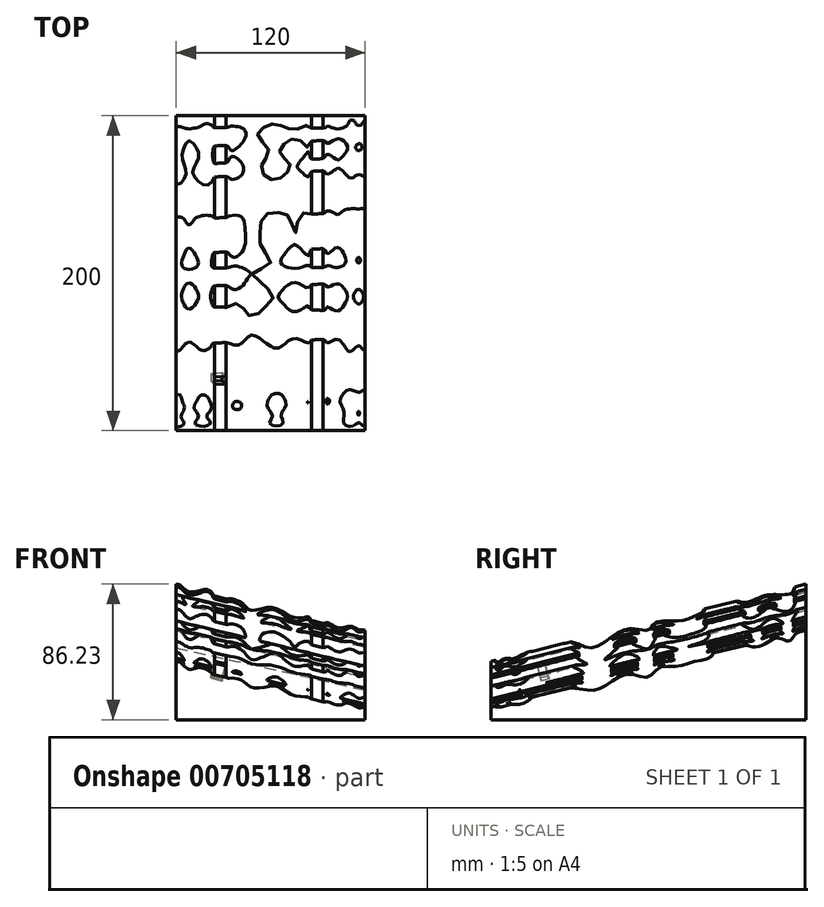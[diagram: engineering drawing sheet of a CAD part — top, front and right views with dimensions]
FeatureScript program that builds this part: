
annotation { "Feature Type Name" : "Feature", "Feature Type Description" : "" }
export const myFeature = defineFeature(function(context is Context, id is Id, definition is map)
    precondition{}
    {
        {
            var Q0;
            Q0=qCreatedBy(makeId("Top.planeOp"),FACE);
            var sketch = newSketch(context, id + "F0", { "sketchPlane" : qUnion([Q0])});
            skLineSegment(sketch, "E0.bottom", {"start": v(-60, -100) * mm, "end": v(60, -100) * mm});
            skLineSegment(sketch, "E0.top", {"start": v(-60, 100) * mm, "end": v(60, 100) * mm});
            skLineSegment(sketch, "E0.left", {"start": v(-60, -100) * mm, "end": v(-60, 100) * mm});
            skLineSegment(sketch, "E0.right", {"start": v(60, -100) * mm, "end": v(60, 100) * mm});
            skLineSegment(sketch, "E1", {"start": v(0, 100) * mm, "end": v(0, -100) * mm, "construction": true});
            skSolve(sketch);
        }
        {
            var Q0;
            Q0=sQuery(id+"F0.wireOp",VERTEX,"E0.right.start");
            var Q1;
            Q1=qCreatedBy(makeId("Front.planeOp"),FACE);
            cPlane(context, id + "F1", {"entities" : qUnion([Q0, Q1]), "cplaneType" : CPlaneType.PLANE_POINT, "offset" : 25 * mm, "width" : 150 * mm, "height" : 150 * mm});
        }
        {
            var Q0;
            Q0=sQuery(id+"F0.wireOp",VERTEX,"E0.right.start");
            var Q1;
            Q1=qCreatedBy(makeId("Right.planeOp"),FACE);
            cPlane(context, id + "F2", {"entities" : qUnion([Q0, Q1]), "cplaneType" : CPlaneType.PLANE_POINT, "offset" : 25 * mm, "width" : 150 * mm, "height" : 150 * mm});
        }
        {
            var Q0;
            Q0=sQuery(id+"F0.wireOp",VERTEX,"E0.right.end");
            var Q1;
            Q1=qCreatedBy(makeId("Front.planeOp"),FACE);
            cPlane(context, id + "F3", {"entities" : qUnion([Q0, Q1]), "cplaneType" : CPlaneType.PLANE_POINT, "offset" : 25 * mm, "width" : 150 * mm, "height" : 150 * mm});
        }
        {
            var Q0;
            Q0=sQuery(id+"F0.wireOp",VERTEX,"E0.bottom.start");
            var Q1;
            Q1=qCreatedBy(makeId("Right.planeOp"),FACE);
            cPlane(context, id + "F4", {"entities" : qUnion([Q0, Q1]), "cplaneType" : CPlaneType.PLANE_POINT, "offset" : 25 * mm, "width" : 150 * mm, "height" : 150 * mm});
        }
        {
            var Q0;
            Q0=qCreatedBy(id+"F1.planeOp",FACE);
            var sketch = newSketch(context, id + "F5", { "sketchPlane" : qUnion([Q0])});
            skPoint(sketch, "E2.0", {"position": v(60, 0) * mm});
            skLineSegment(sketch, "E3", {"start": v(60, 0) * mm, "end": v(60, 10) * mm});
            skPoint(sketch, "E4.0", {"position": v(-60, 0) * mm});
            skLineSegment(sketch, "E5", {"start": v(-60, 0) * mm, "end": v(-60, 40) * mm});
            skLineSegment(sketch, "E6", {"start": v(-60, 40) * mm, "end": v(60, 10) * mm});
            skLineSegment(sketch, "E7.0", {"start": v(-60, 0) * mm, "end": v(60, 0) * mm});
            skSolve(sketch);
        }
        {
            var Q0;
            Q0=qCreatedBy(id+"F2.planeOp",FACE);
            var sketch = newSketch(context, id + "F6", { "sketchPlane" : qUnion([Q0])});
            skPoint(sketch, "E8.0", {"position": v(-100, 10) * mm});
            skPoint(sketch, "E9.0", {"position": v(100, 0) * mm});
            skLineSegment(sketch, "E10", {"start": v(-100, 10) * mm, "end": v(100, 60) * mm});
            skLineSegment(sketch, "E11", {"start": v(100, 60) * mm, "end": v(100, 0) * mm});
            skLineSegment(sketch, "E12.0", {"start": v(-100, 0) * mm, "end": v(-100, 10) * mm});
            skLineSegment(sketch, "E13.0", {"start": v(-100, 0) * mm, "end": v(100, 0) * mm});
            skSolve(sketch);
        }
        {
            var Q0;
            Q0=qCreatedBy(id+"F3.planeOp",FACE);
            var sketch = newSketch(context, id + "F7", { "sketchPlane" : qUnion([Q0])});
            skPoint(sketch, "E14.0", {"position": v(60, 60) * mm});
            skPoint(sketch, "E15.0", {"position": v(-60, 0) * mm});
            skLineSegment(sketch, "E16", {"start": v(60, 60) * mm, "end": v(-60, 90) * mm});
            skLineSegment(sketch, "E17", {"start": v(-60, 90) * mm, "end": v(-60, 0) * mm});
            skLineSegment(sketch, "E18.0", {"start": v(60, 60) * mm, "end": v(60, 0) * mm});
            skLineSegment(sketch, "E19.0", {"start": v(-60, 0) * mm, "end": v(60, 0) * mm});
            skSolve(sketch);
        }
        {
            var Q0;
            Q0=qCreatedBy(id+"F4.planeOp",FACE);
            var sketch = newSketch(context, id + "F8", { "sketchPlane" : qUnion([Q0])});
            skPoint(sketch, "E20.0", {"position": v(100, 90) * mm});
            skPoint(sketch, "E21.0", {"position": v(-100, 40) * mm});
            skLineSegment(sketch, "E22", {"start": v(100, 90) * mm, "end": v(-100, 40) * mm});
            skLineSegment(sketch, "E23.0", {"start": v(100, 90) * mm, "end": v(100, 0) * mm});
            skLineSegment(sketch, "E24.0", {"start": v(-100, 0) * mm, "end": v(100, 0) * mm});
            skLineSegment(sketch, "E25.0", {"start": v(-100, 0) * mm, "end": v(-100, 40) * mm});
            skSolve(sketch);
        }
        {
            var Q0;
            Q0=makeQuery(id+"F8.imprint","IMPRINT",FACE,{"disambiguationData":[TD([[makeQuery(id+"F8.imprint","IMPRINT",EDGE,{"derivedFrom":sQuery(id+"F8.wireOp",EDGE,"E22")}),1.0]])]});
            var Q1;
            Q1=makeQuery(id+"F6.imprint","IMPRINT",FACE,{"disambiguationData":[TD([[makeQuery(id+"F6.imprint","IMPRINT",EDGE,{"derivedFrom":sQuery(id+"F6.wireOp",EDGE,"E10")}),-1.0]])]});
            loft(context, id + "F9", {"sheetProfilesArray" : [{ "sheetProfileEntities" : qUnion([Q0]) }, { "sheetProfileEntities" : qUnion([Q1]) }]});
        }
        {
            var Q0;
            Q0=makeQuery(id+"F9.opLoft","SWEPT_FACE",FACE,{"disambiguationData":[OSD([sQuery(id+"F6.wireOp",EDGE,"E10"),sQuery(id+"F6.wireOp",EDGE,"E11"),sQuery(id+"F6.wireOp",EDGE,"E12.0"),sQuery(id+"F8.wireOp",EDGE,"E22"),sQuery(id+"F8.wireOp",EDGE,"E23.0"),sQuery(id+"F8.wireOp",EDGE,"E25.0")])]});
            var sketch = newSketch(context, id + "F10", { "sketchPlane" : qUnion([Q0])});
            skLineSegment(sketch, "E26.left", {"start": v(-46.93, 117.3) * mm, "end": v(-46.93, -93.87) * mm});
            skLineSegment(sketch, "E26.right", {"start": v(-39.43, 116.85) * mm, "end": v(-39.43, -94.3) * mm});
            skLineSegment(sketch, "E27.left", {"start": v(16.57, 113.55) * mm, "end": v(16.57, -94.3) * mm});
            skLineSegment(sketch, "E27.right", {"start": v(24.07, 113.11) * mm, "end": v(24.07, -94.75) * mm});
            skPoint(sketch, "E28.0", {"position": v(-11.43, -90.95) * mm});
            skLineSegment(sketch, "E29", {"start": v(-46.93, 11.71) * mm, "end": v(24.07, 11.71) * mm, "construction": true});
            skLineSegment(sketch, "E30", {"start": v(-11.43, -90.95) * mm, "end": v(-11.43, 11.71) * mm, "construction": true});
            skLineSegment(sketch, "E31.0", {"start": v(-73.17, 118.84) * mm, "end": v(50.3, 111.57) * mm});
            skLineSegment(sketch, "E32.0", {"start": v(-73.17, -87.31) * mm, "end": v(50.3, -94.59) * mm});
            skLineSegment(sketch, "E33", {"start": v(-46.93, -93.87) * mm, "end": v(-39.43, -94.3) * mm});
            skLineSegment(sketch, "E34", {"start": v(16.57, -94.3) * mm, "end": v(24.07, -94.75) * mm});
            skLineSegment(sketch, "E35", {"start": v(-46.93, 117.3) * mm, "end": v(-39.43, 116.85) * mm});
            skLineSegment(sketch, "E36", {"start": v(16.57, 113.55) * mm, "end": v(24.07, 113.11) * mm});
            skSolve(sketch);
        }
        {
            var Q0;
            Q0=makeQuery(id+"F10.imprint","IMPRINT",FACE,{"disambiguationData":[TD([[makeQuery(id+"F10.imprint","IMPRINT",EDGE,{"derivedFrom":sQuery(id+"F10.wireOp",EDGE,"E26.bottom")}),-1.0]])]});
            var Q1;
            Q1=makeQuery(id+"F10.imprint","IMPRINT",FACE,{"disambiguationData":[TD([[makeQuery(id+"F10.imprint","IMPRINT",EDGE,{"derivedFrom":sQuery(id+"F10.wireOp",EDGE,"E27.bottom")}),-1.0]])]});
            var Q2;
            Q2=makeQuery(id+"F10.imprint","IMPRINT",FACE,{"disambiguationData":[TD([[makeQuery(id+"F10.imprint","IMPRINT",EDGE,{"derivedFrom":sQuery(id+"F10.wireOp",EDGE,"NEKn6sk2-oqBZ-cDOU-tW9F-8VQi9Gtyu4y1.bottom")}),-1.0]])]});
            var Q3;
            Q3=makeQuery(id+"F10.imprint","IMPRINT",FACE,{"disambiguationData":[TD([[makeQuery(id+"F10.imprint","IMPRINT",EDGE,{"derivedFrom":sQuery(id+"F10.wireOp",EDGE,"wy3WmLDI-bbM7-1tcg-6uRk-hKdkDB1jThqP.bottom")}),-1.0]])]});
            var Q4;
            Q4=makeQuery(id+"F10.imprint","IMPRINT",FACE,{"disambiguationData":[TD([[makeQuery(id+"F10.imprint","IMPRINT",EDGE,{"derivedFrom":sQuery(id+"F10.wireOp",EDGE,"NEKn6sk2-oqBZ-cDOU-tW9F-8VQi9Gtyu4y1.top")}),-1.0]])]});
            var Q5;
            Q5=makeQuery(id+"F10.imprint","IMPRINT",FACE,{"disambiguationData":[TD([[makeQuery(id+"F10.imprint","IMPRINT",EDGE,{"derivedFrom":sQuery(id+"F10.wireOp",EDGE,"wy3WmLDI-bbM7-1tcg-6uRk-hKdkDB1jThqP.top")}),-1.0]])]});
            var Q6;
            Q6=makeQuery(id+"F10.imprint","IMPRINT",FACE,{"disambiguationData":[TD([[makeQuery(id+"F10.imprint","IMPRINT",EDGE,{"derivedFrom":sQuery(id+"F10.wireOp",EDGE,"E26.top")}),1.0]])]});
            var Q7;
            Q7=makeQuery(id+"F10.imprint","IMPRINT",FACE,{"disambiguationData":[TD([[makeQuery(id+"F10.imprint","IMPRINT",EDGE,{"derivedFrom":sQuery(id+"F10.wireOp",EDGE,"E27.top")}),1.0]])]});
            var Q8;
            Q8=makeQuery(id+"F10.imprint","IMPRINT",FACE,{"disambiguationData":[TD([[makeQuery(id+"F10.imprint","IMPRINT",EDGE,{"derivedFrom":sQuery(id+"F10.wireOp",EDGE,"E26.left")}),1.0]])]});
            var Q9;
            Q9=makeQuery(id+"F10.imprint","IMPRINT",FACE,{"disambiguationData":[TD([[makeQuery(id+"F10.imprint","IMPRINT",EDGE,{"derivedFrom":sQuery(id+"F10.wireOp",EDGE,"E27.left")}),1.0]])]});
            extrude(context, id + "F11", {"entities" : qUnion([Q0, Q1, Q2, Q3, Q4, Q5, Q6, Q7, Q8, Q9]), "operationType" : NewBodyOperationType.REMOVE, "oppositeDirection" : true, "depth" : 5 * mm, "offsetDistance" : 25 * mm});
        }
        {
            var Q0;
            Q0=makeQuery(id+"F11.boolean.opBoolean","COPY",FACE,{"derivedFrom":makeQuery(id+"F11.opExtrude","CAP_FACE",FACE,{"disambiguationData":[OSD([sQuery(id+"F10.wireOp",EDGE,"E26.left"),sQuery(id+"F10.wireOp",EDGE,"E26.right"),sQuery(id+"F10.wireOp",EDGE,"E33"),sQuery(id+"F10.wireOp",EDGE,"E35")])],"isStart":false})});
            var sketch = newSketch(context, id + "F12", { "sketchPlane" : qUnion([Q0])});
            skLineSegment(sketch, "E37.0", {"start": v(-46.93, 116.08) * mm, "end": v(-46.93, -90.07) * mm});
            skLineSegment(sketch, "E38.0", {"start": v(-39.43, 115.64) * mm, "end": v(-39.43, -90.52) * mm});
            skLineSegment(sketch, "E39.bottom", {"start": v(-46.93, -55.07) * mm, "end": v(-39.43, -55.07) * mm});
            skLineSegment(sketch, "E39.top", {"start": v(-46.93, -60.07) * mm, "end": v(-39.43, -60.07) * mm});
            skLineSegment(sketch, "E39.left", {"start": v(-46.93, -55.07) * mm, "end": v(-46.93, -60.07) * mm});
            skLineSegment(sketch, "E39.right", {"start": v(-39.43, -55.07) * mm, "end": v(-39.43, -60.07) * mm});
            skSolve(sketch);
        }
        {
            var Q0;
            Q0=makeQuery(id+"F12.imprint","IMPRINT",FACE,{"disambiguationData":[TD([[makeQuery(id+"F12.imprint","IMPRINT",EDGE,{"derivedFrom":sQuery(id+"F12.wireOp",EDGE,"E39.bottom")}),-1.0]])]});
            extrude(context, id + "F13", {"entities" : qUnion([Q0]), "operationType" : NewBodyOperationType.REMOVE, "oppositeDirection" : true, "depth" : 10 * mm, "offsetDistance" : 25 * mm});
        }
        {
            var Q0;
            Q0=makeQuery(id+"F9.opLoft","CAP_FACE",FACE,{"disambiguationData":[OSD([makeQuery(id+"F6.imprint","IMPRINT",FACE,{"disambiguationData":[TD([[makeQuery(id+"F6.imprint","IMPRINT",EDGE,{"derivedFrom":sQuery(id+"F6.wireOp",EDGE,"E10")}),-1.0]])]})])],"isStart":true});
            var sketch = newSketch(context, id + "F14", { "sketchPlane" : qUnion([Q0])});
            skLineSegment(sketch, "E40", {"start": v(-60, 20) * mm, "end": v(-70, 17.5) * mm});
            skLineSegment(sketch, "E41", {"start": v(45, 46.25) * mm, "end": v(55, 48.75) * mm});
            skFitSpline(sketch, "E42", {"points": [v(-60, 20) * mm, v(-44.37, 19.8) * mm, v(-32.93, 19.12) * mm, v(-22.08, 25.24) * mm, v(-10.69, 29.05) * mm, v(-0.1, 27.13) * mm, v(6.57, 33.14) * mm, v(18.25, 33.85) * mm, v(27.64, 36.6) * mm, v(37.34, 38.8) * mm, v(41, 41.63) * mm, v(45, 46.25) * mm], "startDerivative": vector(98.1, 24.52) * mm, "endDerivative": vector(170.9, 42.72) * mm});
            skLineSegment(sketch, "E43.0", {"start": v(100, 60) * mm, "end": v(-100, 10) * mm});
            skFitSpline(sketch, "E44", {"points": [v(55, 48.75) * mm, v(69.35, 46.37) * mm, v(81.14, 52) * mm, v(89.4, 50.18) * mm, v(93.67, 54.7) * mm, v(98.2, 57.05) * mm, v(100, 60) * mm], "startDerivative": vector(30.97, 7.74) * mm, "endDerivative": vector(26.44, 6.61) * mm});
            skFitSpline(sketch, "E45", {"points": [v(-100, 10) * mm, v(-97.5, 8.72) * mm, v(-94, 8.1) * mm, v(-87.27, 9.82) * mm, v(-81.18, 10.02) * mm, v(-74.84, 13.43) * mm, v(-70, 17.5) * mm], "startDerivative": vector(29.52, 7.38) * mm, "endDerivative": vector(26.31, 6.58) * mm});
            skLineSegment(sketch, "E46", {"start": v(-65, 18.75) * mm, "end": v(-65, 40.23) * mm, "construction": true});
            skLineSegment(sketch, "E47", {"start": v(50, 47.5) * mm, "end": v(50, 75.28) * mm, "construction": true});
            skSolve(sketch);
        }
        {
            var Q0;
            Q0=makeQuery(id+"F9.opLoft","CAP_FACE",FACE,{"disambiguationData":[OSD([makeQuery(id+"F8.imprint","IMPRINT",FACE,{"disambiguationData":[TD([[makeQuery(id+"F8.imprint","IMPRINT",EDGE,{"derivedFrom":sQuery(id+"F8.wireOp",EDGE,"E22")}),1.0]])]})])],"isStart":true});
            var sketch = newSketch(context, id + "F15", { "sketchPlane" : qUnion([Q0])});
            skLineSegment(sketch, "E48", {"start": v(75, 46.25) * mm, "end": v(65, 48.75) * mm});
            skLineSegment(sketch, "E49", {"start": v(-40, 75) * mm, "end": v(-50, 77.5) * mm});
            skFitSpline(sketch, "E50", {"points": [v(65, 48.75) * mm, v(48.83, 49.59) * mm, v(36.64, 45.72) * mm, v(23.85, 52.4) * mm, v(11.73, 57.9) * mm, v(-0.39, 57.03) * mm, v(-4.05, 61.71) * mm, v(-15.2, 62.65) * mm, v(-24.44, 63.93) * mm, v(-31.93, 66.98) * mm, v(-35.06, 69.46) * mm, v(-40, 75) * mm], "startDerivative": vector(-108.82, 27.2) * mm, "endDerivative": vector(-139.64, 34.91) * mm});
            skFitSpline(sketch, "E51", {"points": [v(75, 46.25) * mm, v(76.94, 43.31) * mm, v(80.88, 41.2) * mm, v(86.05, 38.8) * mm, v(91.22, 38.96) * mm, v(96.34, 36.7) * mm, v(100, 40) * mm], "startDerivative": vector(29.03, -7.26) * mm, "endDerivative": vector(25.06, -6.27) * mm});
            skLineSegment(sketch, "E52", {"start": v(100, 40) * mm, "end": v(75, 46.25) * mm});
            skFitSpline(sketch, "E53", {"points": [v(-50, 77.5) * mm, v(-60.32, 74.54) * mm, v(-72.9, 78.66) * mm, v(-83.8, 79.44) * mm, v(-91.25, 80.87) * mm, v(-93.27, 84.98) * mm, v(-100, 90) * mm], "startDerivative": vector(-30.07, 7.52) * mm, "endDerivative": vector(-22.2, 4.63) * mm});
            skLineSegment(sketch, "E54", {"start": v(-50, 77.5) * mm, "end": v(-100, 90) * mm});
            skLineSegment(sketch, "E55", {"start": v(70, 47.5) * mm, "end": v(70, 79) * mm, "construction": true});
            skLineSegment(sketch, "E56", {"start": v(-45, 76.25) * mm, "end": v(-45, 101.04) * mm, "construction": true});
            skSolve(sketch);
        }
        {
            var Q1;
            Q1=makeQuery(id+"F15.imprint","IMPRINT",FACE,{"disambiguationData":[TD([[makeQuery(id+"F15.imprint","IMPRINT",EDGE,{"derivedFrom":sQuery(id+"F15.wireOp",EDGE,"E51")}),1.0]])]});
            var Q2;
            {var subQ2=sQuery(id+"F14.wireOp",EDGE,"E45");Q2=makeQuery(id+"F14.imprint","IMPRINT",FACE,{"disambiguationData":[TD([[makeQuery(id+"F14.imprint","IMPRINT",EDGE,{"derivedFrom":subQ2}),1.0]])]});}
            loft(context, id + "F16", {"operationType" : NewBodyOperationType.REMOVE, "sheetProfilesArray" : [{ "sheetProfileEntities" : qUnion([Q1]) }, { "sheetProfileEntities" : qUnion([Q2]) }]});
        }
        {
            var Q1;
            {var subQ0=sQuery(id+"F15.wireOp",EDGE,"E50");Q1=makeQuery(id+"F15.imprint","IMPRINT",FACE,{"disambiguationData":[TD([[makeQuery(id+"F15.imprint","IMPRINT",EDGE,{"derivedFrom":subQ0}),-1.0]])]});}
            var Q2;
            {var subQ0=sQuery(id+"F14.wireOp",EDGE,"E42");Q2=makeQuery(id+"F14.imprint","IMPRINT",FACE,{"disambiguationData":[TD([[makeQuery(id+"F14.imprint","IMPRINT",EDGE,{"derivedFrom":subQ0}),1.0]])]});}
            loft(context, id + "F17", {"operationType" : NewBodyOperationType.REMOVE, "sheetProfilesArray" : [{ "sheetProfileEntities" : qUnion([Q1]) }, { "sheetProfileEntities" : qUnion([Q2]) }]});
        }
        {
            var Q1;
            Q1=makeQuery(id+"F15.imprint","IMPRINT",FACE,{"disambiguationData":[TD([[makeQuery(id+"F15.imprint","IMPRINT",EDGE,{"derivedFrom":sQuery(id+"F15.wireOp",EDGE,"E53")}),-1.0]])]});
            var Q2;
            {var subQ2=sQuery(id+"F14.wireOp",EDGE,"E44");Q2=makeQuery(id+"F14.imprint","IMPRINT",FACE,{"disambiguationData":[TD([[makeQuery(id+"F14.imprint","IMPRINT",EDGE,{"derivedFrom":subQ2}),1.0]])]});}
            loft(context, id + "F18", {"operationType" : NewBodyOperationType.REMOVE, "sheetProfilesArray" : [{ "sheetProfileEntities" : qUnion([Q1]) }, { "sheetProfileEntities" : qUnion([Q2]) }]});
        }
        {
            var Q0;
            Q0=makeQuery(id+"F9.opLoft","SWEPT_FACE",FACE,{"disambiguationData":[OSD([sQuery(id+"F6.wireOp",EDGE,"E10"),sQuery(id+"F6.wireOp",EDGE,"E12.0"),sQuery(id+"F6.wireOp",EDGE,"E13.0"),sQuery(id+"F8.wireOp",EDGE,"E22"),sQuery(id+"F8.wireOp",EDGE,"E24.0"),sQuery(id+"F8.wireOp",EDGE,"E25.0")])]});
            var sketch = newSketch(context, id + "F19", { "sketchPlane" : qUnion([Q0])});
            skLineSegment(sketch, "E57.0", {"start": v(-28.39, 26.8) * mm, "end": v(-35.68, 28.62) * mm});
            skLineSegment(sketch, "E58.0", {"start": v(33.32, 11.37) * mm, "end": v(26.03, 13.19) * mm});
            skFitSpline(sketch, "E59", {"points": [v(-60, 37.1) * mm, v(-55.92, 35.18) * mm, v(-51.74, 32.09) * mm, v(-45.27, 33.17) * mm, v(-37.8, 29.93) * mm, v(-35.68, 28.62) * mm], "startDerivative": vector(24.65, 4.99) * mm, "endDerivative": vector(35.4, -8.85) * mm});
            skFitSpline(sketch, "E60", {"points": [v(-28.39, 26.8) * mm, v(-23.53, 26.48) * mm, v(-17.69, 24.74) * mm, v(-10.84, 20.25) * mm, v(3.3, 21.33) * mm, v(14.27, 15.62) * mm, v(23.82, 14.4) * mm, v(26.03, 13.19) * mm], "startDerivative": vector(52.46, -15.21) * mm, "endDerivative": vector(53.86, -13.46) * mm});
            skFitSpline(sketch, "E61", {"points": [v(33.32, 11.37) * mm, v(35.62, 11.6) * mm, v(42.75, 9.36) * mm, v(49.4, 10.65) * mm, v(56.1, 7.68) * mm, v(60, 8.05) * mm], "startDerivative": vector(37.91, -9.48) * mm, "endDerivative": vector(21.78, -2.74) * mm});
            skLineSegment(sketch, "E62.0", {"start": v(27.21, 18.2) * mm, "end": v(26.03, 13.19) * mm});
            skLineSegment(sketch, "E63.0", {"start": v(34.5, 16.38) * mm, "end": v(33.32, 11.37) * mm});
            skFitSpline(sketch, "E64.0", {"points": [v(-27.21, 31.8) * mm, v(-9.07, 27.27) * mm, v(9.07, 22.73) * mm, v(27.21, 18.2) * mm]});
            skLineSegment(sketch, "E65.0", {"start": v(-27.21, 31.8) * mm, "end": v(-28.39, 26.8) * mm});
            skLineSegment(sketch, "E66.0", {"start": v(-34.5, 33.62) * mm, "end": v(-35.68, 28.62) * mm});
            skFitSpline(sketch, "E67.0", {"points": [v(-60, 40) * mm, v(-51.5, 37.87) * mm, v(-43, 35.75) * mm, v(-34.5, 33.62) * mm]});
            skLineSegment(sketch, "E68.0", {"start": v(-60, 40) * mm, "end": v(-60, 0) * mm});
            skLineSegment(sketch, "E69.0", {"start": v(60, 10) * mm, "end": v(60, 0) * mm});
            skSolve(sketch);
        }
        {
            var Q0;
            Q0=makeQuery(id+"F9.opLoft","SWEPT_FACE",FACE,{"disambiguationData":[OSD([sQuery(id+"F6.wireOp",EDGE,"E10"),sQuery(id+"F6.wireOp",EDGE,"E11"),sQuery(id+"F6.wireOp",EDGE,"E13.0"),sQuery(id+"F8.wireOp",EDGE,"E22"),sQuery(id+"F8.wireOp",EDGE,"E23.0"),sQuery(id+"F8.wireOp",EDGE,"E24.0")])]});
            var sketch = newSketch(context, id + "F20", { "sketchPlane" : qUnion([Q0])});
            skLineSegment(sketch, "E70.0", {"start": v(-26.03, 63.19) * mm, "end": v(-33.32, 61.37) * mm});
            skLineSegment(sketch, "E71.0", {"start": v(35.68, 78.62) * mm, "end": v(28.39, 76.8) * mm});
            skLineSegment(sketch, "E72.0", {"start": v(-60, 0) * mm, "end": v(-60, 60) * mm});
            skFitSpline(sketch, "E73", {"points": [v(-60, 56.77) * mm, v(-56.05, 57.25) * mm, v(-50.83, 59.43) * mm, v(-43.68, 58.32) * mm, v(-35.8, 61.79) * mm, v(-33.32, 61.37) * mm], "startDerivative": vector(20.35, 12.67) * mm, "endDerivative": vector(25.57, 6.4) * mm});
            skFitSpline(sketch, "E74", {"points": [v(-26.03, 63.19) * mm, v(-24.32, 65.23) * mm, v(-19.73, 64.8) * mm, v(-11.73, 66.14) * mm, v(-0.36, 71.4) * mm, v(12.3, 69.4) * mm, v(17.45, 73.3) * mm, v(25.92, 77.04) * mm, v(28.39, 76.8) * mm], "startDerivative": vector(40.48, 10.12) * mm, "endDerivative": vector(44.62, 11.15) * mm});
            skFitSpline(sketch, "E75", {"points": [v(35.68, 78.62) * mm, v(37.1, 80.53) * mm, v(40.86, 82.85) * mm, v(45, 82.06) * mm, v(52.68, 81.65) * mm, v(57.86, 85.74) * mm, v(60, 86.23) * mm], "startDerivative": vector(14.81, 3.7) * mm, "endDerivative": vector(14.73, 5.36) * mm});
            skLineSegment(sketch, "E76.0", {"start": v(-34.5, 66.38) * mm, "end": v(-60, 60) * mm});
            skPoint(sketch, "E77.0", {"position": v(-26.62, 65.7) * mm});
            skLineSegment(sketch, "E78.0", {"start": v(-26.03, 63.19) * mm, "end": v(-27.21, 68.2) * mm});
            skLineSegment(sketch, "E79.0", {"start": v(27.21, 81.8) * mm, "end": v(-27.21, 68.2) * mm});
            skLineSegment(sketch, "E80.0", {"start": v(28.39, 76.8) * mm, "end": v(27.21, 81.8) * mm});
            skLineSegment(sketch, "E81.0", {"start": v(35.68, 78.62) * mm, "end": v(34.5, 83.62) * mm});
            skLineSegment(sketch, "E82.0", {"start": v(60, 90) * mm, "end": v(34.5, 83.62) * mm});
            skLineSegment(sketch, "E83.0", {"start": v(60, 0) * mm, "end": v(60, 90) * mm});
            skLineSegment(sketch, "E84.0", {"start": v(-33.32, 61.37) * mm, "end": v(-34.5, 66.38) * mm});
            skSolve(sketch);
        }
        {
            var Q1;
            {var subQ0=sQuery(id+"F19.wireOp",EDGE,"E59");Q1=makeQuery(id+"F19.imprint","IMPRINT",FACE,{"disambiguationData":[TD([[makeQuery(id+"F19.imprint","IMPRINT",EDGE,{"derivedFrom":subQ0}),1.0]])]});}
            var Q2;
            {var subQ0=sQuery(id+"F20.wireOp",EDGE,"E75");Q2=makeQuery(id+"F20.imprint","IMPRINT",FACE,{"disambiguationData":[TD([[makeQuery(id+"F20.imprint","IMPRINT",EDGE,{"derivedFrom":subQ0}),1.0]])]});}
            loft(context, id + "F21", {"operationType" : NewBodyOperationType.REMOVE, "sheetProfilesArray" : [{ "sheetProfileEntities" : qUnion([Q1]) }, { "sheetProfileEntities" : qUnion([Q2]) }]});
        }
        {
            var Q1;
            Q1=makeQuery(id+"F19.imprint","IMPRINT",FACE,{"disambiguationData":[TD([[makeQuery(id+"F19.imprint","IMPRINT",EDGE,{"derivedFrom":sQuery(id+"F19.wireOp",EDGE,"E60")}),1.0]])]});
            var Q2;
            Q2=makeQuery(id+"F20.imprint","IMPRINT",FACE,{"disambiguationData":[TD([[makeQuery(id+"F20.imprint","IMPRINT",EDGE,{"derivedFrom":sQuery(id+"F20.wireOp",EDGE,"E74")}),1.0]])]});
            loft(context, id + "F22", {"operationType" : NewBodyOperationType.REMOVE, "sheetProfilesArray" : [{ "sheetProfileEntities" : qUnion([Q1]) }, { "sheetProfileEntities" : qUnion([Q2]) }]});
        }
        {
            var Q1;
            {var subQ0=sQuery(id+"F19.wireOp",EDGE,"E61");Q1=makeQuery(id+"F19.imprint","IMPRINT",FACE,{"disambiguationData":[TD([[makeQuery(id+"F19.imprint","IMPRINT",EDGE,{"derivedFrom":subQ0}),1.0]])]});}
            var Q2;
            {var subQ0=sQuery(id+"F20.wireOp",EDGE,"E76.0");Q2=makeQuery(id+"F20.imprint","IMPRINT",FACE,{"disambiguationData":[TD([[makeQuery(id+"F20.imprint","IMPRINT",EDGE,{"derivedFrom":subQ0}),1.0]])]});}
            loft(context, id + "F23", {"operationType" : NewBodyOperationType.REMOVE, "sheetProfilesArray" : [{ "sheetProfileEntities" : qUnion([Q1]) }, { "sheetProfileEntities" : qUnion([Q2]) }]});
        }
    });
